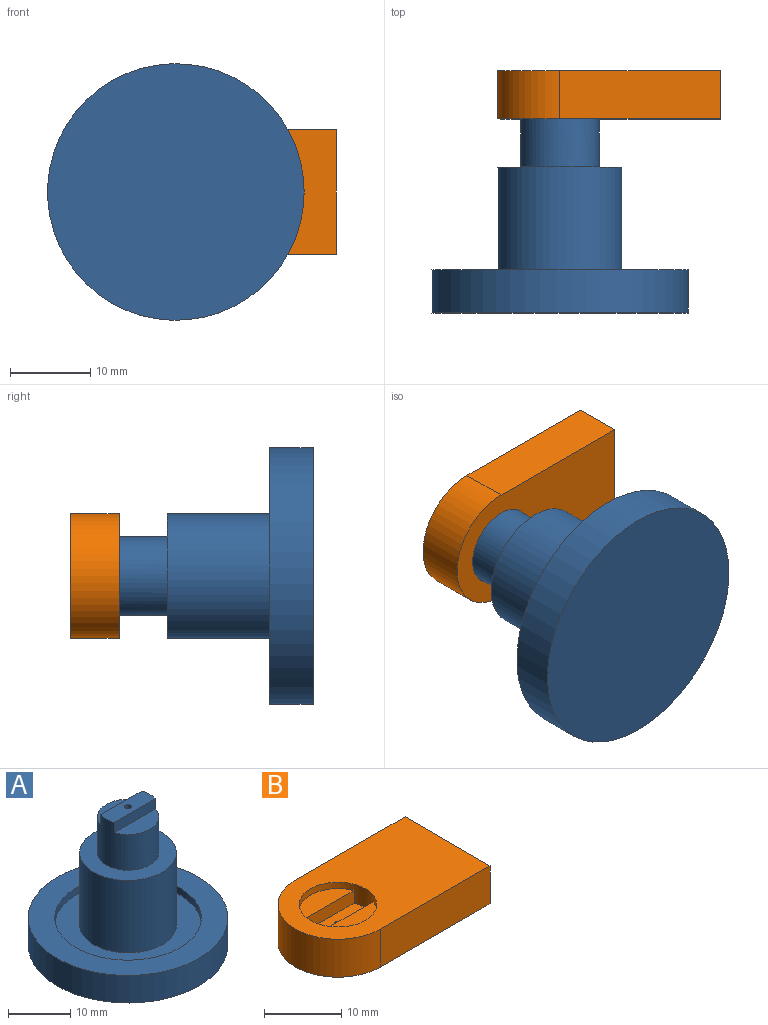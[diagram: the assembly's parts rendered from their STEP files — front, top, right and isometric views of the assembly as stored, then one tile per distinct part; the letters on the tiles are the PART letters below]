
ASSEMBLY  parts=2 mates=1
PART A: 15 faces, bbox 32x32x27.2 mm
  f0: plane 9.8x3mm, normal (0,0,1), area 28mm2, adj f4,f5,f7,f9
  f1: plane 23.5x23.5mm, normal (0,0,1), area 245mm2, adj f2,f11
  f2: cylinder r=7.75mm len=15.5mm, axis (0,0,-1), area 691.5mm2, adj f1,f3
  f3: plane 15.5x15.5mm, normal (0,0,1), area 113.3mm2, adj f2,f4
  f4: cylinder r=4.9mm len=9.8mm, axis (0,0,-1), area 227.7mm2, adj f0,f3,f5,f6,f7,f8
  f5: plane 9.33x2mm, normal (0,-1,0), area 18.7mm2, adj f0,f4,f6
  f6: plane 9.33x3.4mm, normal (0,0,1), area 23.2mm2, adj f4,f5
  f7: plane 9.33x2mm, normal (0,1,0), area 18.7mm2, adj f0,f4,f8
  f8: plane 9.33x3.4mm, normal (0,0,1), area 23.2mm2, adj f4,f7
  f9: cylinder r=0.55mm len=10mm, axis (0,0,1), area 34.7mm2, adj f0,f10
  f10: plane 1.11x1.11mm, normal (0,0,1), area 1mm2, adj f9
  f11: cylinder r=11.75mm len=23.5mm, axis (0,0,-1), area 103.4mm2, adj f1,f12
  f12: plane 32x32mm, normal (0,0,1), area 370.5mm2, adj f11,f14
  f13: plane 32x32mm, normal (0,0,-1), area 804.2mm2, adj f14
  f14: cylinder r=16mm len=32mm, axis (0,0,-1), area 542.9mm2, adj f12,f13
PART B: 13 faces, bbox 27.8x15.5x6 mm
  f0: cylinder r=0.5mm len=3mm, axis (0,0,-1), area 9.4mm2, adj f7,f10
  f1: plane 9.37x3.25mm, normal (0,0,1), area 22.1mm2, adj f9,f11
  f2: plane 15.5x6mm, normal (1,0,0), area 93mm2, adj f3,f5,f6,f7
  f3: plane 20x6mm, normal (0,1,0), area 120mm2, adj f2,f4,f6,f7
  f4: cylinder r=7.75mm len=15.5mm, axis (0,0,-1), area 146.1mm2, adj f3,f5,f6,f7
  f5: plane 20x6mm, normal (0,-1,0), area 120mm2, adj f2,f4,f6,f7
  f6: plane 27.75x15.5mm, normal (0,0,1), area 325.8mm2, adj f2,f3,f4,f5,f9
  f7: plane 27.75x15.5mm, normal (0,0,-1), area 403.6mm2, adj f0,f2,f3,f4,f5
  f8: plane 9.37x3.25mm, normal (0,0,1), area 22.1mm2, adj f9,f12
  f9: cylinder r=5mm len=10mm, axis (0,0,1), area 45.7mm2, adj f1,f6,f8,f10,f11,f12
  f10: plane 10x3.5mm, normal (0,0,1), area 33.5mm2, adj f0,f9,f11,f12
  f11: plane 9.37x2mm, normal (0,1,0), area 18.7mm2, adj f1,f9,f10
  f12: plane 9.37x2mm, normal (0,-1,0), area 18.7mm2, adj f8,f9,f10
PLACE A rot(axis=(-1,0,0),90deg) t=(-55.57,-69.16,12.23)mm
PLACE B rot(axis=(1,0,0),90deg) t=(-62.4,-38.96,4)mm
MATE fastened A.f2 <-> B.f0  axis (0,1,0) through (-62.4,-41.96,4)mm
